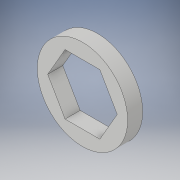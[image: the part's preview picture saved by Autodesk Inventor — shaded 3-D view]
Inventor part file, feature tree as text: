
AUTODESK INVENTOR PART (.ipt)
format: ipt  version: 2018 (Build 220112000, 112)  size: 103,936 bytes
history: native  units: in
note: dims shown in document units (in); Inventor stores cm internally (conversion verified against a paired STEP export)
features: extrude x1, sketch x1
ambient origin geometry x8: Origin, YZ Plane, XZ Plane, XY Plane, X Axis, Y Axis, Z Axis, Center Point
bodies: Solid1 (feature_tree)
feature tree (2):
  extrude  "Extrusion1"  Depth=0.125in
  sketch  "Sketch1"  dims[d0=0.5in d1=0.75in d2=0.125in d3=0.0in]
